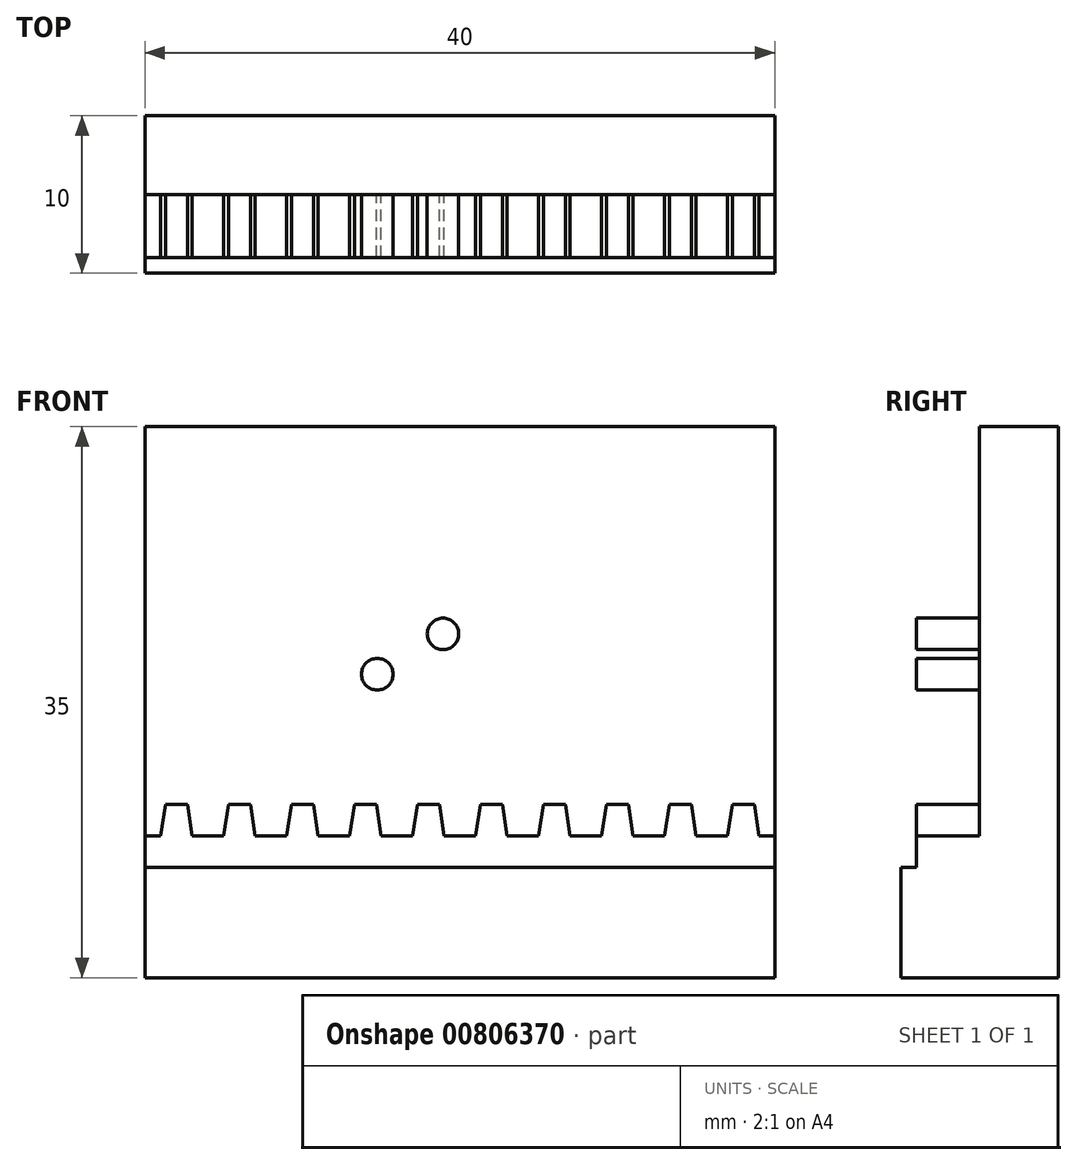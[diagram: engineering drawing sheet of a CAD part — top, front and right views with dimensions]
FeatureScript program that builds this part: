
annotation { "Feature Type Name" : "Feature", "Feature Type Description" : "" }
export const myFeature = defineFeature(function(context is Context, id is Id, definition is map)
    precondition{}
    {
        {
            var Q0;
            Q0=qCreatedBy(makeId("Front.planeOp"),FACE);
            var sketch = newSketch(context, id + "F0", { "sketchPlane" : qUnion([Q0])});
            skLineSegment(sketch, "E0.bottom", {"start": v(-20, 17.5) * mm, "end": v(20, 17.5) * mm});
            skLineSegment(sketch, "E0.top", {"start": v(-20, -17.5) * mm, "end": v(20, -17.5) * mm});
            skLineSegment(sketch, "E0.left", {"start": v(-20, 17.5) * mm, "end": v(-20, -17.5) * mm});
            skLineSegment(sketch, "E0.right", {"start": v(20, 17.5) * mm, "end": v(20, -17.5) * mm});
            skPoint(sketch, "E0.middle", {"position": v(0, 0) * mm});
            skSolve(sketch);
        }
        {
            var Q0;
            Q0 = qSketchRegion(id + "F0", true);
            extrude(context, id + "F1", {"entities" : qUnion([Q0]), "depth" : 10 * mm, "offsetDistance" : 25 * mm});
        }
        {
            var Q0;
            Q0=makeQuery(id+"F1.opExtrude","CAP_FACE",FACE,{"disambiguationData":[OSD([sQuery(id+"F0.wireOp",EDGE,"E0.bottom"),sQuery(id+"F0.wireOp",EDGE,"E0.top"),sQuery(id+"F0.wireOp",EDGE,"E0.left"),sQuery(id+"F0.wireOp",EDGE,"E0.right")])],"isStart":false});
            var sketch = newSketch(context, id + "F2", { "sketchPlane" : qUnion([Q0])});
            skLineSegment(sketch, "E1.bottom", {"start": v(-20, 17.5) * mm, "end": v(20, 17.5) * mm});
            skLineSegment(sketch, "E1.top", {"start": v(-20, -12.5) * mm, "end": v(20, -12.5) * mm});
            skLineSegment(sketch, "E1.left", {"start": v(-20, 17.5) * mm, "end": v(-20, -12.5) * mm});
            skLineSegment(sketch, "E1.right", {"start": v(20, 17.5) * mm, "end": v(20, -12.5) * mm});
            skSolve(sketch);
        }
        {
            var Q0;
            Q0 = qSketchRegion(id + "F2", true);
            extrude(context, id + "F3", {"entities" : qUnion([Q0]), "operationType" : NewBodyOperationType.REMOVE, "oppositeDirection" : true, "depth" : 5 * mm, "offsetDistance" : 25 * mm});
        }
        {
            var Q0;
            Q0=makeQuery(id+"F1.opExtrude","SWEPT_FACE",FACE,{"disambiguationData":[OSD([sQuery(id+"F0.wireOp",EDGE,"E0.right")])]});
            var sketch = newSketch(context, id + "F4", { "sketchPlane" : qUnion([Q0])});
            skLineSegment(sketch, "E2.bottom", {"start": v(-10, -12.5) * mm, "end": v(-9, -12.5) * mm});
            skLineSegment(sketch, "E2.top", {"start": v(-10, -10.5) * mm, "end": v(-9, -10.5) * mm});
            skLineSegment(sketch, "E2.left", {"start": v(-10, -12.5) * mm, "end": v(-10, -10.5) * mm});
            skLineSegment(sketch, "E2.right", {"start": v(-9, -12.5) * mm, "end": v(-9, -10.5) * mm});
            skSolve(sketch);
        }
        {
            var Q0;
            Q0 = qSketchRegion(id + "F4", true);
            var Q1;
            Q1=makeQuery(id+"F1.opExtrude","SWEPT_FACE",FACE,{"disambiguationData":[OSD([sQuery(id+"F0.wireOp",EDGE,"E0.left")])]});
            extrude(context, id + "F5", {"entities" : qUnion([Q0]), "operationType" : NewBodyOperationType.ADD, "endBound" : BoundingType.UP_TO_SURFACE, "oppositeDirection" : true, "depth" : 25 * mm, "endBoundEntityFace" : qUnion([Q1]), "offsetDistance" : 25 * mm});
        }
        {
            var Q0;
            Q0=makeQuery(id+"F3.boolean.opBoolean","COPY",FACE,{"derivedFrom":makeQuery(id+"F3.opExtrude","CAP_FACE",FACE,{"disambiguationData":[OSD([sQuery(id+"F2.wireOp",EDGE,"E1.bottom"),sQuery(id+"F2.wireOp",EDGE,"E1.top"),sQuery(id+"F2.wireOp",EDGE,"E1.left"),sQuery(id+"F2.wireOp",EDGE,"E1.right")])],"isStart":false})});
            var sketch = newSketch(context, id + "F6", { "sketchPlane" : qUnion([Q0])});
            skCircle(sketch, "E3", {"center": v(-1.07, 4.34) * mm, "radius": 1 * mm});
            skCircle(sketch, "E4", {"center": v(-5.24, 1.78) * mm, "radius": 1 * mm});
            skSolve(sketch);
        }
        {
            var Q0;
            Q0 = qSketchRegion(id + "F6", true);
            extrude(context, id + "F7", {"entities" : qUnion([Q0]), "operationType" : NewBodyOperationType.ADD, "depth" : 4 * mm, "offsetDistance" : 25 * mm});
        }
        {
            var Q0;
            Q0=makeQuery(id+"F3.boolean.opBoolean","COPY",FACE,{"derivedFrom":makeQuery(id+"F3.opExtrude","CAP_FACE",FACE,{"disambiguationData":[OSD([sQuery(id+"F2.wireOp",EDGE,"E1.bottom"),sQuery(id+"F2.wireOp",EDGE,"E1.top"),sQuery(id+"F2.wireOp",EDGE,"E1.left"),sQuery(id+"F2.wireOp",EDGE,"E1.right")])],"isStart":false})});
            var sketch = newSketch(context, id + "F8", { "sketchPlane" : qUnion([Q0])});
            skLineSegment(sketch, "E5.bottom", {"start": v(20, -12.5) * mm, "end": v(-20, -12.5) * mm});
            skLineSegment(sketch, "E5.top", {"start": v(20, -8.5) * mm, "end": v(-20, -8.5) * mm});
            skLineSegment(sketch, "E5.left", {"start": v(20, -12.5) * mm, "end": v(20, -8.5) * mm});
            skLineSegment(sketch, "E5.right", {"start": v(-20, -12.5) * mm, "end": v(-20, -8.5) * mm});
            skLineSegment(sketch, "E6", {"start": v(-18, -8.5) * mm, "end": v(-18, -12.5) * mm, "construction": true});
            skLineSegment(sketch, "E7", {"start": v(-19, -8.5) * mm, "end": v(-18.7, -6.5) * mm});
            skLineSegment(sketch, "E8", {"start": v(-18.7, -6.5) * mm, "end": v(-18, -6.5) * mm});
            skLineSegment(sketch, "E9.MirrorCS", {"start": v(-17, -8.5) * mm, "end": v(-17.3, -6.5) * mm});
            skLineSegment(sketch, "E10.MirrorCS", {"start": v(-17.3, -6.5) * mm, "end": v(-18, -6.5) * mm});
            skLineSegment(sketch, "E11.1.0.0", {"start": v(-15, -8.5) * mm, "end": v(-14.7, -6.5) * mm});
            skLineSegment(sketch, "E11.1.0.1", {"start": v(-14.7, -6.5) * mm, "end": v(-14, -6.5) * mm});
            skLineSegment(sketch, "E11.1.0.2", {"start": v(-13.3, -6.5) * mm, "end": v(-14, -6.5) * mm});
            skLineSegment(sketch, "E11.1.0.3", {"start": v(-13, -8.5) * mm, "end": v(-13.3, -6.5) * mm});
            skLineSegment(sketch, "E11.2.0.0", {"start": v(-11, -8.5) * mm, "end": v(-10.7, -6.5) * mm});
            skLineSegment(sketch, "E11.2.0.1", {"start": v(-10.7, -6.5) * mm, "end": v(-10, -6.5) * mm});
            skLineSegment(sketch, "E11.2.0.2", {"start": v(-9.3, -6.5) * mm, "end": v(-10, -6.5) * mm});
            skLineSegment(sketch, "E11.2.0.3", {"start": v(-9, -8.5) * mm, "end": v(-9.3, -6.5) * mm});
            skLineSegment(sketch, "E11.3.0.0", {"start": v(-7, -8.5) * mm, "end": v(-6.7, -6.5) * mm});
            skLineSegment(sketch, "E11.3.0.1", {"start": v(-6.7, -6.5) * mm, "end": v(-6, -6.5) * mm});
            skLineSegment(sketch, "E11.3.0.2", {"start": v(-5.3, -6.5) * mm, "end": v(-6, -6.5) * mm});
            skLineSegment(sketch, "E11.3.0.3", {"start": v(-5, -8.5) * mm, "end": v(-5.3, -6.5) * mm});
            skLineSegment(sketch, "E11.4.0.0", {"start": v(-3, -8.5) * mm, "end": v(-2.7, -6.5) * mm});
            skLineSegment(sketch, "E11.4.0.1", {"start": v(-2.7, -6.5) * mm, "end": v(-2, -6.5) * mm});
            skLineSegment(sketch, "E11.4.0.2", {"start": v(-1.3, -6.5) * mm, "end": v(-2, -6.5) * mm});
            skLineSegment(sketch, "E11.4.0.3", {"start": v(-1, -8.5) * mm, "end": v(-1.3, -6.5) * mm});
            skLineSegment(sketch, "E11.5.0.0", {"start": v(1, -8.5) * mm, "end": v(1.3, -6.5) * mm});
            skLineSegment(sketch, "E11.5.0.1", {"start": v(1.3, -6.5) * mm, "end": v(2, -6.5) * mm});
            skLineSegment(sketch, "E11.5.0.2", {"start": v(2.7, -6.5) * mm, "end": v(2, -6.5) * mm});
            skLineSegment(sketch, "E11.5.0.3", {"start": v(3, -8.5) * mm, "end": v(2.7, -6.5) * mm});
            skLineSegment(sketch, "E11.6.0.0", {"start": v(5, -8.5) * mm, "end": v(5.3, -6.5) * mm});
            skLineSegment(sketch, "E11.6.0.1", {"start": v(5.3, -6.5) * mm, "end": v(6, -6.5) * mm});
            skLineSegment(sketch, "E11.6.0.2", {"start": v(6.7, -6.5) * mm, "end": v(6, -6.5) * mm});
            skLineSegment(sketch, "E11.6.0.3", {"start": v(7, -8.5) * mm, "end": v(6.7, -6.5) * mm});
            skLineSegment(sketch, "E11.7.0.0", {"start": v(9, -8.5) * mm, "end": v(9.3, -6.5) * mm});
            skLineSegment(sketch, "E11.7.0.1", {"start": v(9.3, -6.5) * mm, "end": v(10, -6.5) * mm});
            skLineSegment(sketch, "E11.7.0.2", {"start": v(10.7, -6.5) * mm, "end": v(10, -6.5) * mm});
            skLineSegment(sketch, "E11.7.0.3", {"start": v(11, -8.5) * mm, "end": v(10.7, -6.5) * mm});
            skLineSegment(sketch, "E11.8.0.0", {"start": v(13, -8.5) * mm, "end": v(13.3, -6.5) * mm});
            skLineSegment(sketch, "E11.8.0.1", {"start": v(13.3, -6.5) * mm, "end": v(14, -6.5) * mm});
            skLineSegment(sketch, "E11.8.0.2", {"start": v(14.7, -6.5) * mm, "end": v(14, -6.5) * mm});
            skLineSegment(sketch, "E11.8.0.3", {"start": v(15, -8.5) * mm, "end": v(14.7, -6.5) * mm});
            skLineSegment(sketch, "E11.9.0.0", {"start": v(17, -8.5) * mm, "end": v(17.3, -6.5) * mm});
            skLineSegment(sketch, "E11.9.0.1", {"start": v(17.3, -6.5) * mm, "end": v(18, -6.5) * mm});
            skLineSegment(sketch, "E11.9.0.2", {"start": v(18.7, -6.5) * mm, "end": v(18, -6.5) * mm});
            skLineSegment(sketch, "E11.9.0.3", {"start": v(19, -8.5) * mm, "end": v(18.7, -6.5) * mm});
            skLineSegment(sketch, "E11.direction1", {"start": v(-19, -8.5) * mm, "end": v(-15, -8.5) * mm, "construction": true});
            skSolve(sketch);
        }
        {
            var Q0;
            Q0 = qSketchRegion(id + "F8", true);
            extrude(context, id + "F9", {"entities" : qUnion([Q0]), "operationType" : NewBodyOperationType.ADD, "depth" : 4 * mm, "offsetDistance" : 25 * mm});
        }
        {
            var Q0;
            Q0=makeQuery(id+"F1.opExtrude","SWEPT_BODY",BODY,{"disambiguationData":[OSD([sQuery(id+"F0.wireOp",EDGE,"E0.bottom"),sQuery(id+"F0.wireOp",EDGE,"E0.top"),sQuery(id+"F0.wireOp",EDGE,"E0.left"),sQuery(id+"F0.wireOp",EDGE,"E0.right")])]});
            transform(context, id + "F10", {"entities" : qUnion([Q0]), "transformType" : TransformType.TRANSLATION_3D, "dx" : 0 * mm, "dy" : 0 * mm, "dz" : 0 * mm, "makeCopy" : true});
        }
        {
            var Q0;
            Q0=makeQuery(id+"F1.opExtrude","SWEPT_BODY",BODY,{"disambiguationData":[OSD([sQuery(id+"F0.wireOp",EDGE,"E0.bottom"),sQuery(id+"F0.wireOp",EDGE,"E0.top"),sQuery(id+"F0.wireOp",EDGE,"E0.left"),sQuery(id+"F0.wireOp",EDGE,"E0.right")])]});
            deleteBodies(context, id + "F11", {"entities" : qUnion([Q0])});
        }
    });
